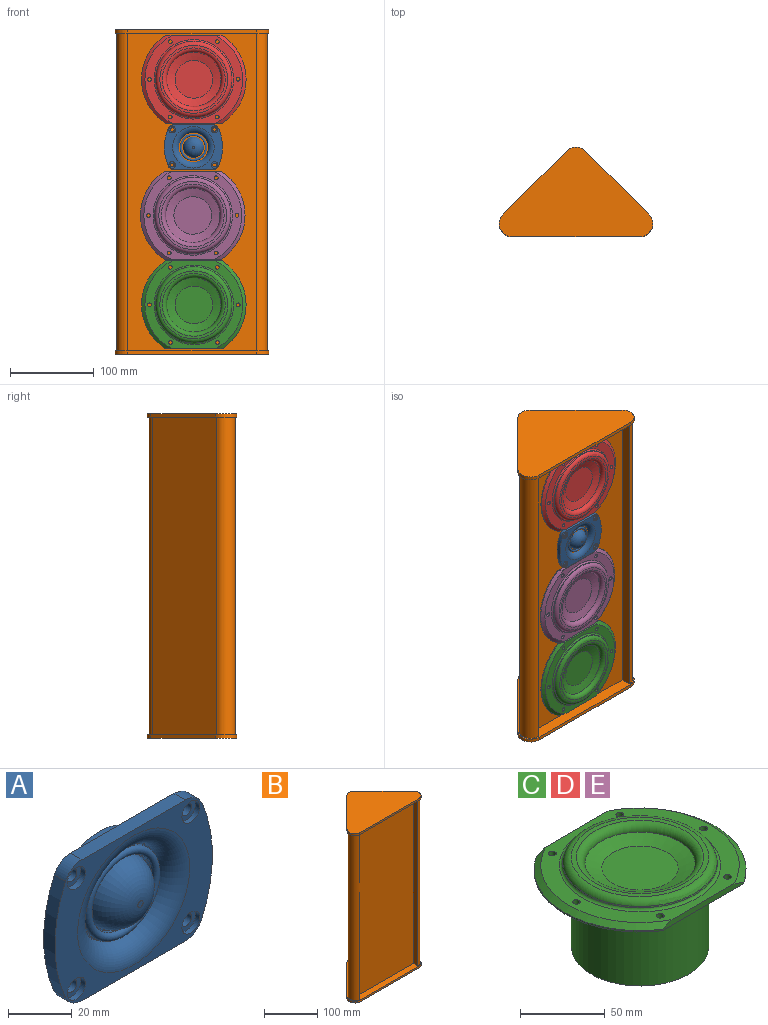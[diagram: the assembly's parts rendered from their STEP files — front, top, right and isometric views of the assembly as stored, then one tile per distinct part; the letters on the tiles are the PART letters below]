
ASSEMBLY  parts=5 mates=4
PART A: 33 faces, bbox 69.7x18x54 mm
  f0: plane 45.68x5mm, normal (0,0,-1), area 228.4mm2, adj f4,f5,f17,f20
  f1: cylinder r=55mm len=44.47mm, axis (0,1,0), area 228.9mm2, adj f4,f5,f17,f18
  f2: plane 45.68x5mm, normal (0,0,1), area 228.4mm2, adj f4,f5,f18,f19
  f3: cylinder r=55mm len=44.47mm, axis (0,1,0), area 228.9mm2, adj f4,f5,f19,f20
  f4: plane 69.7x54mm, normal (0,-1,0), area 1365.2mm2, adj f0,f1,f2,f3,f10,f17,f18,f19
  f5: plane 69.7x54mm, normal (0,1,0), area 1625.4mm2, adj f0,f1,f2,f3,f8,f17,f18,f19
  f6: cylinder r=19mm len=38mm, axis (0,-1,0), area 596.9mm2, adj f7,f8
  f7: plane 38x38mm, normal (0,1,0), area 1134.1mm2, adj f6
  f8: torus R=24mm, axis (0,-1,0), area 1027.3mm2, adj f5,f6
  f9: plane 34x34mm, normal (0,-1,0), area 52.6mm2, adj f10,f11
  f10: torus R=24.8mm, axis (0,-1,0), area 1443.3mm2, adj f4,f9
  f11: cylinder r=16.5mm len=33mm, axis (0,1,0), area 155.5mm2, adj f9,f14
  f12: cylinder r=13.5mm len=27mm, axis (0,-1,0), area 127.2mm2, adj f13,f14
  f13: plane 27x27mm, normal (0,-1,0), area 41.6mm2, adj f12,f16
  f14: torus R=15mm, axis (0,-1,0), area 444.1mm2, adj f11,f12
  f15: plane 2.34x2.34mm, normal (0,-1,0), area 4.3mm2, adj f16
  f16: torus R=1.17mm, axis (0,1,0), area 877.6mm2, adj f13,f15
  f17: cylinder r=8mm len=7.32mm, axis (0,1,0), area 46.2mm2, adj f0,f1,f4,f5
  f18: cylinder r=8mm len=7.32mm, axis (0,1,0), area 46.2mm2, adj f1,f2,f4,f5
  f19: cylinder r=8mm len=7.32mm, axis (0,1,0), area 46.2mm2, adj f2,f3,f4,f5
  f20: cylinder r=8mm len=7.32mm, axis (0,1,0), area 46.2mm2, adj f0,f3,f4,f5
  f21: cylinder r=4mm len=8mm, axis (0,-1,0), area 50.3mm2, adj f4,f22
  f22: plane 8x8mm, normal (0,-1,0), area 34.4mm2, adj f21,f32
  f23: cylinder r=4mm len=8mm, axis (0,-1,0), area 50.3mm2, adj f4,f24
  f24: plane 8x8mm, normal (0,-1,0), area 34.4mm2, adj f23,f31
  f25: cylinder r=4mm len=8mm, axis (0,-1,0), area 50.3mm2, adj f4,f26
  f26: plane 8x8mm, normal (0,-1,0), area 34.4mm2, adj f25,f30
  f27: cylinder r=4mm len=8mm, axis (0,-1,0), area 50.3mm2, adj f4,f28
  f28: plane 8x8mm, normal (0,-1,0), area 34.4mm2, adj f27,f29
  f29: cylinder r=2.25mm len=4.5mm, axis (0,-1,0), area 42.4mm2, adj f5,f28
  f30: cylinder r=2.25mm len=4.5mm, axis (0,-1,0), area 42.4mm2, adj f5,f26
  f31: cylinder r=2.25mm len=4.5mm, axis (0,-1,0), area 42.4mm2, adj f5,f24
  f32: cylinder r=2.25mm len=4.5mm, axis (0,-1,0), area 42.4mm2, adj f5,f22
PART B: 24 faces, bbox 183.8x106.9x388 mm
  f0: plane 76.92x76.92mm, normal (0.71,0.71,0), area 435.1mm2, adj f3,f4,f5,f7
  f1: plane 76.92x76.92mm, normal (-0.71,0.71,0), area 435.1mm2, adj f3,f4,f5,f6
  f2: plane 153.85x4mm, normal (0,-1,0), area 615.4mm2, adj f3,f4,f6,f7
  f3: plane 183.85x106.92mm, normal (0,0,1), area 2764.9mm2, adj f0,f1,f2,f5,f6,f7,f8,f9
  f4: plane 183.85x106.92mm, normal (0,0,-1), area 12195.5mm2, adj f0,f1,f2,f5,f6,f7
  f5: cylinder r=15mm len=21.21mm, axis (0,0,-1), area 94.2mm2, adj f0,f1,f3,f4
  f6: cylinder r=15mm len=25.61mm, axis (0,0,-1), area 141.4mm2, adj f1,f2,f3,f4
  f7: cylinder r=15mm len=25.61mm, axis (0,0,-1), area 141.4mm2, adj f0,f2,f3,f4
  f8: plane 380x76.92mm, normal (-0.71,0.71,0), area 41339mm2, adj f3,f10,f11,f17
  f9: plane 380x76.92mm, normal (0.71,0.71,0), area 41339mm2, adj f3,f10,f12,f17
  f10: cylinder r=13mm len=380mm, axis (0,0,-1), area 7759.7mm2, adj f3,f8,f9,f17
  f11: cylinder r=13mm len=380mm, axis (0,0,-1), area 11639.6mm2, adj f3,f8,f17,f21
  f12: cylinder r=13mm len=380mm, axis (0,0,-1), area 11639.6mm2, adj f3,f9,f17,f22
  f13: plane 153.85x4mm, normal (0,-1,0), area 615.4mm2, adj f16,f17,f18,f20
  f14: plane 76.92x76.92mm, normal (0.71,0.71,0), area 435.1mm2, adj f16,f17,f18,f19
  f15: plane 76.92x76.92mm, normal (-0.71,0.71,0), area 435.1mm2, adj f16,f17,f19,f20
  f16: plane 183.85x106.92mm, normal (0,0,1), area 12195.5mm2, adj f13,f14,f15,f18,f19,f20
  f17: plane 183.85x106.92mm, normal (0,0,-1), area 2764.9mm2, adj f8,f9,f10,f11,f12,f13,f14,f15
  f18: cylinder r=15mm len=25.61mm, axis (0,0,-1), area 141.4mm2, adj f13,f14,f16,f17
  f19: cylinder r=15mm len=21.21mm, axis (0,0,-1), area 94.2mm2, adj f14,f15,f16,f17
  f20: cylinder r=15mm len=25.61mm, axis (0,0,-1), area 141.4mm2, adj f13,f15,f16,f17
  f21: plane 380x12mm, normal (1,0,0), area 4560mm2, adj f3,f11,f17,f23
  f22: plane 380x12mm, normal (-1,0,0), area 4560mm2, adj f3,f12,f17,f23
  f23: plane 380x153.85mm, normal (0,-1,0), area 58462.2mm2, adj f3,f17,f21,f22
PART C: 23 faces, bbox 125x112.2x64.5 mm
  f0: cylinder r=62.5mm len=105mm, axis (0,0,-1), area 124.7mm2, adj f3,f4,f13,f14
  f1: cylinder r=62.5mm len=105mm, axis (0,0,-1), area 124.7mm2, adj f3,f5,f13,f14
  f2: plane 117x105mm, normal (0,0,1), area 3140mm2, adj f4,f5,f9,f13,f14,f15,f16,f17
  f3: plane 125x105mm, normal (0,0,-1), area 6103.6mm2, adj f0,f1,f13,f14,f15,f16,f17,f18
  f4: cone r=58.5mm half-angle=53.1deg, axis (0,0,-1), area 636.3mm2, adj f0,f2,f13,f14
  f5: cone r=58.5mm half-angle=53.1deg, axis (0,0,-1), area 636.3mm2, adj f1,f2,f13,f14
  f6: cone r=46mm half-angle=15deg, axis (0,0,-1), area 240.2mm2, adj f9,f10
  f7: plane 81.11x81.11mm, normal (0,0,1), area 749.3mm2, adj f10,f11
  f8: plane 45x45mm, normal (0,0,1), area 1590.4mm2, adj f12
  f9: torus R=47.53mm, axis (0,0,1), area 763.3mm2, adj f2,f6
  f10: torus R=40.56mm, axis (0,0,1), area 1784.2mm2, adj f6,f7
  f11: torus R=37.5mm, axis (0,0,1), area 1693.5mm2, adj f7,f12
  f12: cone r=22.5mm half-angle=73.3deg, axis (0,0,1), area 1804mm2, adj f8,f11
  f13: plane 67.83x4mm, normal (0,-1,0), area 247.8mm2, adj f0,f1,f2,f3,f4,f5
  f14: plane 67.83x4mm, normal (0,1,0), area 247.8mm2, adj f0,f1,f2,f3,f4,f5
  f15: cylinder r=2.25mm len=4.5mm, axis (0,0,1), area 56.5mm2, adj f2,f3
  f16: cylinder r=2.25mm len=4.5mm, axis (0,0,1), area 56.5mm2, adj f2,f3
  f17: cylinder r=2.25mm len=4.5mm, axis (0,0,1), area 56.5mm2, adj f2,f3
  f18: cylinder r=2.25mm len=4.5mm, axis (0,0,1), area 56.5mm2, adj f2,f3
  f19: cylinder r=2.25mm len=4.5mm, axis (0,0,1), area 56.5mm2, adj f2,f3
  f20: cylinder r=2.25mm len=4.5mm, axis (0,0,1), area 56.5mm2, adj f2,f3
  f21: cylinder r=40.5mm len=81mm, axis (0,0,1), area 13868.6mm2, adj f3,f22
  f22: plane 81x81mm, normal (0,0,-1), area 5153mm2, adj f21
PART D: same geometry as C
PART E: same geometry as C
PLACE A rot(axis=(0,0,1),0deg) t=(1.7,-36,247.4)mm
PLACE B at identity fixed
PLACE C rot(axis=(1,0,0),90deg) t=(2.18,-36,59.07)mm
PLACE D rot(axis=(1,0,0),90deg) t=(2.18,-36,328.73)mm
PLACE E rot(axis=(1,0,0),90deg) t=(0.91,-36,166)mm
MATE planar B.f23 <-> A.f20  axis (0,-1,0) through (0,-36,194)mm
MATE planar E.f15 <-> B.f23  axis (0,1,0) through (29,-36,121.05)mm
MATE planar B.f23 <-> D.f0  axis (0,-1,0) through (0,-36,194)mm
MATE planar C.f0 <-> B.f23  axis (0,1,0) through (2.18,-36,59.07)mm
